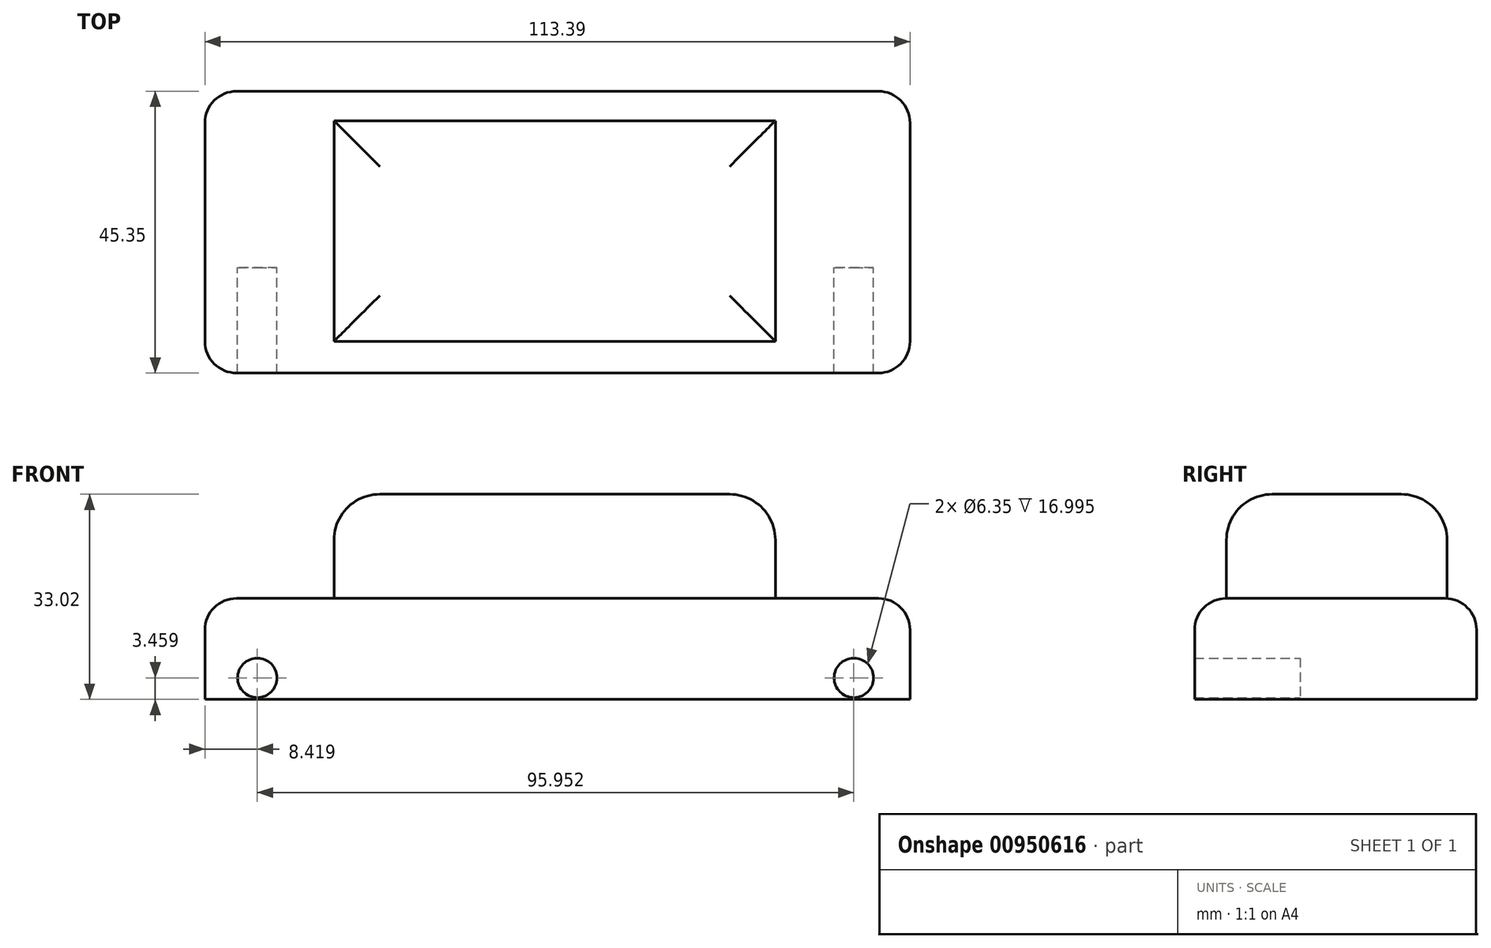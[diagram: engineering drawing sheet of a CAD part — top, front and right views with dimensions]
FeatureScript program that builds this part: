
annotation { "Feature Type Name" : "Feature", "Feature Type Description" : "" }
export const myFeature = defineFeature(function(context is Context, id is Id, definition is map)
    precondition{}
    {
        {
            var Q0;
            Q0=qCreatedBy(makeId("Top.planeOp"),FACE);
            var sketch = newSketch(context, id + "F0", { "sketchPlane" : qUnion([Q0])});
            skLineSegment(sketch, "E0.bottom", {"start": v(-45.6, 28.36) * mm, "end": v(57.63, 28.36) * mm});
            skLineSegment(sketch, "E0.top", {"start": v(-45.6, -17) * mm, "end": v(57.63, -17) * mm});
            skLineSegment(sketch, "E0.left", {"start": v(-50.68, 23.28) * mm, "end": v(-50.68, -11.91) * mm});
            skLineSegment(sketch, "E0.right", {"start": v(62.71, 23.28) * mm, "end": v(62.71, -11.91) * mm});
            skPoint(sketch, "E1.visualSharp", {"position": v(-50.68, 28.36) * mm});
            skArc(sketch, "E1.filletArc", {"start": v(-45.6, 28.36) * mm, "mid": v(-49.2, 26.87) * mm, "end": v(-50.68, 23.28) * mm});
            skPoint(sketch, "E2.visualSharp", {"position": v(-50.68, -17) * mm});
            skArc(sketch, "E2.filletArc", {"start": v(-50.68, -11.91) * mm, "mid": v(-49.2, -15.5) * mm, "end": v(-45.6, -17) * mm});
            skPoint(sketch, "E3.visualSharp", {"position": v(62.71, -17) * mm});
            skArc(sketch, "E3.filletArc", {"start": v(57.63, -17) * mm, "mid": v(61.23, -15.5) * mm, "end": v(62.71, -11.91) * mm});
            skPoint(sketch, "E4.visualSharp", {"position": v(62.71, 28.36) * mm});
            skArc(sketch, "E4.filletArc", {"start": v(62.71, 23.28) * mm, "mid": v(61.23, 26.87) * mm, "end": v(57.63, 28.36) * mm});
            skPoint(sketch, "E5.visualSharp", {"position": v(-28.73, 28.36) * mm});
            skPoint(sketch, "E6.visualSharp", {"position": v(-28.73, -17) * mm});
            skPoint(sketch, "E7.visualSharp", {"position": v(41.96, -17) * mm});
            skPoint(sketch, "E8.visualSharp", {"position": v(41.96, 28.36) * mm});
            skSolve(sketch);
        }
        {
            var Q0;
            Q0 = qSketchRegion(id + "F0", true);
            extrude(context, id + "F1", {"entities" : qUnion([Q0]), "depth" : 16.26 * mm, "offsetDistance" : 25.4 * mm});
        }
        {
            var Q0;
            Q0=makeQuery(id+"F1.opExtrude","CAP_EDGE",EDGE,{"disambiguationData":[OSD([sQuery(id+"F0.wireOp",EDGE,"E2.filletArc")])],"isStart":false});
            fillet(context, id + "F2", {"entities" : qUnion([Q0]), "radius" : 5.08 * mm, "tangentPropagation" : true, "allowEdgeOverflow" : false});
        }
        {
            var Q0;
            Q0=qCreatedBy(makeId("Top.planeOp"),FACE);
            var sketch = newSketch(context, id + "F3", { "sketchPlane" : qUnion([Q0])});
            skLineSegment(sketch, "E9.bottom", {"start": v(-29.93, 23.61) * mm, "end": v(41.06, 23.61) * mm});
            skLineSegment(sketch, "E9.top", {"start": v(-29.93, -11.88) * mm, "end": v(41.06, -11.88) * mm});
            skLineSegment(sketch, "E9.left", {"start": v(-29.93, 23.61) * mm, "end": v(-29.93, -11.88) * mm});
            skLineSegment(sketch, "E9.right", {"start": v(41.06, 23.61) * mm, "end": v(41.06, -11.88) * mm});
            skSolve(sketch);
        }
        {
            var Q0;
            Q0 = qSketchRegion(id + "F3", true);
            extrude(context, id + "F4", {"entities" : qUnion([Q0]), "operationType" : NewBodyOperationType.ADD, "depth" : 33.02 * mm, "offsetDistance" : 25.4 * mm});
        }
        {
            var Q0;
            Q0=makeQuery(id+"F4.opExtrude","CAP_FACE",FACE,{"disambiguationData":[OSD([sQuery(id+"F3.wireOp",EDGE,"E9.bottom"),sQuery(id+"F3.wireOp",EDGE,"E9.top"),sQuery(id+"F3.wireOp",EDGE,"E9.left"),sQuery(id+"F3.wireOp",EDGE,"E9.right")])],"isStart":false});
            fillet(context, id + "F5", {"entities" : qUnion([Q0]), "radius" : 7.36 * mm, "tangentPropagation" : true, "allowEdgeOverflow" : false});
        }
        {
            var Q0;
            Q0=qCreatedBy(makeId("Front.planeOp"),FACE);
            var sketch = newSketch(context, id + "F6", { "sketchPlane" : qUnion([Q0])});
            skLineSegment(sketch, "E10", {"start": v(53.7, 3.46) * mm, "end": v(-42.26, 3.46) * mm});
            skSolve(sketch);
        }
        {
            var Q0;
            Q0=sQuery(id+"F6.wireOp",VERTEX,"E10.start");
            var Q1;
            Q1=sQuery(id+"F6.wireOp",VERTEX,"E10.end");
            var Q2;
            Q2=makeQuery(id+"F1.opExtrude","SWEPT_BODY",BODY,{"disambiguationData":[OSD([sQuery(id+"F0.wireOp",EDGE,"E0.bottom"),sQuery(id+"F0.wireOp",EDGE,"E0.top"),sQuery(id+"F0.wireOp",EDGE,"E0.left"),sQuery(id+"F0.wireOp",EDGE,"E0.right"),sQuery(id+"F0.wireOp",EDGE,"E1.filletArc"),sQuery(id+"F0.wireOp",EDGE,"E2.filletArc"),sQuery(id+"F0.wireOp",EDGE,"E3.filletArc"),sQuery(id+"F0.wireOp",EDGE,"E4.filletArc")])]});
            hole(context, id + "F7", {"style" : HoleStyle.SIMPLE, "endStyle" : HoleEndStyle.THROUGH, "oppositeDirection" : true, "holeDiameter" : 6.35 * mm, "majorDiameter" : 6.35 * mm, "isTappedThrough" : true, "tappedDepth" : 12.7 * mm, "tapClearance" : 3, "locations" : qUnion([Q0, Q1]), "scope" : qUnion([Q2])});
        }
    });
